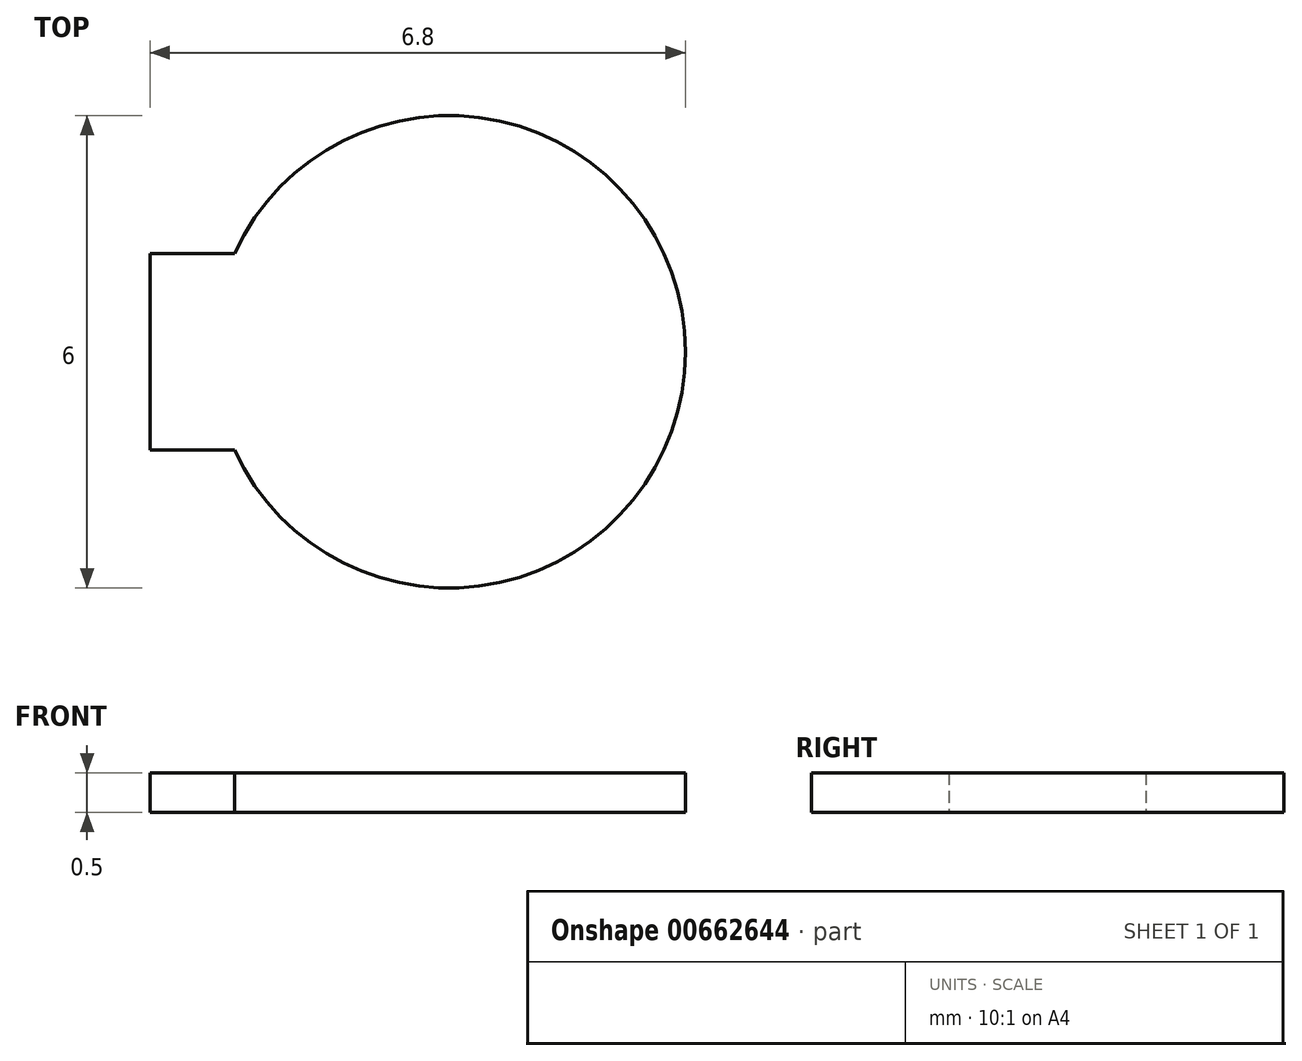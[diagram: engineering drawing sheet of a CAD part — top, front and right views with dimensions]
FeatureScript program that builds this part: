
annotation { "Feature Type Name" : "Feature", "Feature Type Description" : "" }
export const myFeature = defineFeature(function(context is Context, id is Id, definition is map)
    precondition{}
    {
        {
            var Q0;
            Q0=qCreatedBy(makeId("Top.planeOp"),FACE);
            var sketch = newSketch(context, id + "F0", { "sketchPlane" : qUnion([Q0])});
            skArc(sketch, "E0", {"start": v(-2.73, -1.25) * mm, "mid": v(3, 0) * mm, "end": v(-2.73, 1.25) * mm});
            skLineSegment(sketch, "E1", {"start": v(-2.73, 1.25) * mm, "end": v(-3, 1.25) * mm});
            skLineSegment(sketch, "E2", {"start": v(-3, 1.25) * mm, "end": v(-3, 1.25) * mm});
            skLineSegment(sketch, "E3", {"start": v(-3, 1.25) * mm, "end": v(-3.8, 1.25) * mm});
            skLineSegment(sketch, "E4", {"start": v(-3.8, 1.25) * mm, "end": v(-3.8, -1.25) * mm});
            skLineSegment(sketch, "E5", {"start": v(-3.8, -1.25) * mm, "end": v(-3, -1.25) * mm});
            skLineSegment(sketch, "E6", {"start": v(-3, -1.25) * mm, "end": v(-3, -1.25) * mm});
            skLineSegment(sketch, "E7", {"start": v(-3, -1.25) * mm, "end": v(-2.73, -1.25) * mm});
            skSolve(sketch);
        }
        {
            var Q0;
            Q0=makeQuery(id+"F0.imprint","IMPRINT",FACE,{"disambiguationData":[TD([[makeQuery(id+"F0.imprint","IMPRINT",EDGE,{"derivedFrom":sQuery(id+"F0.wireOp",EDGE,"E0")}),1.0]])]});
            extrude(context, id + "F1", {"entities" : qUnion([Q0]), "depth" : .5 * mm, "offsetDistance" : 25 * mm});
        }
    });
